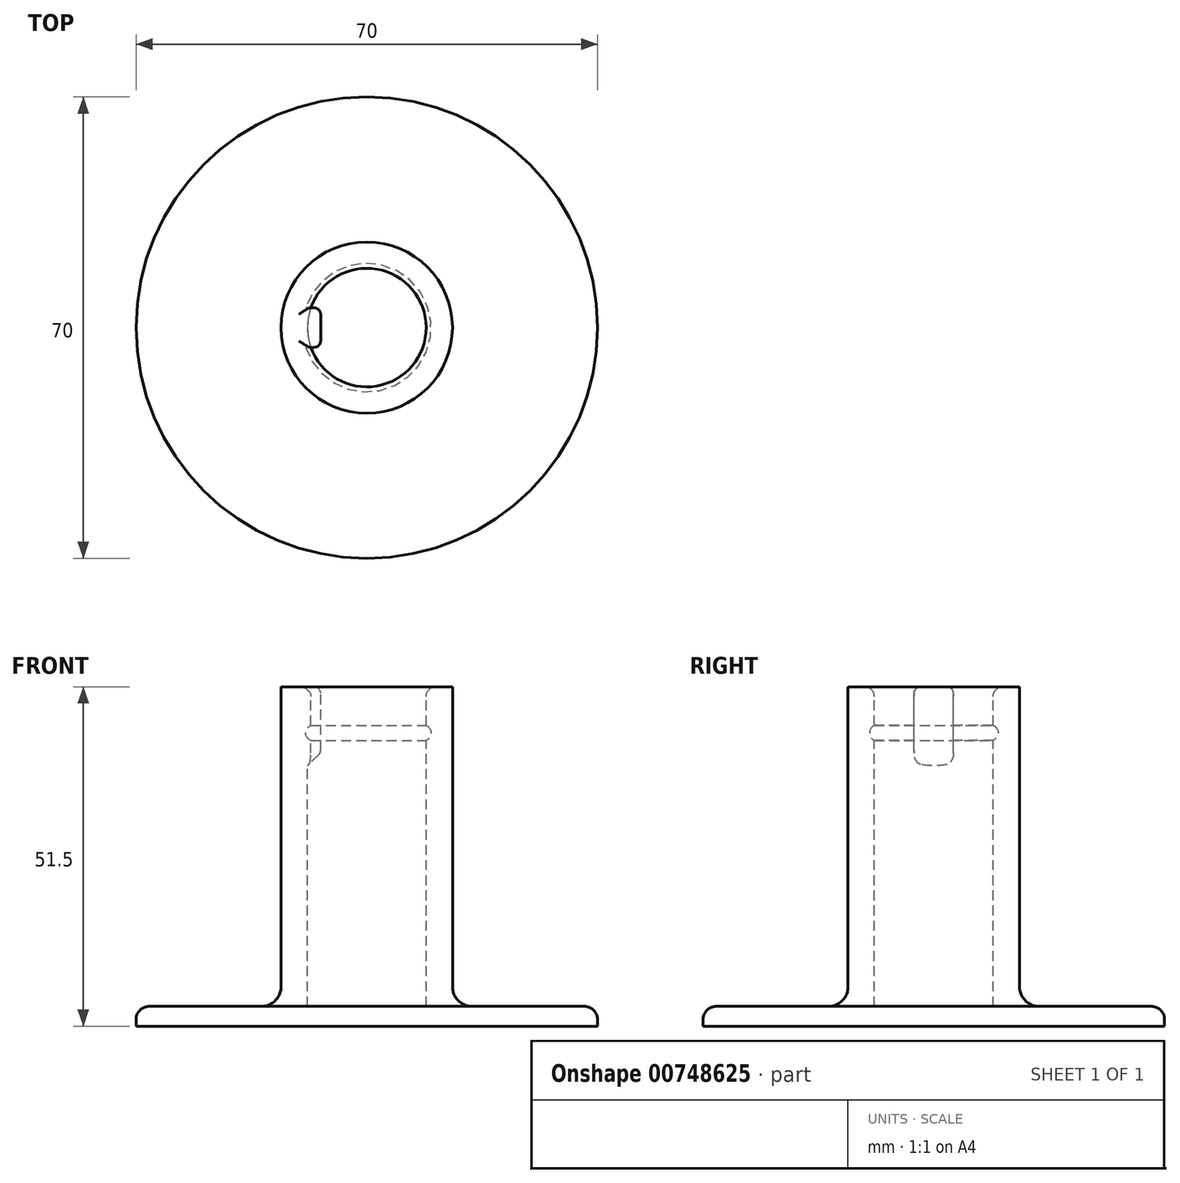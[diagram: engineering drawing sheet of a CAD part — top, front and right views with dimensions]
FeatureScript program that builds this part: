
annotation { "Feature Type Name" : "Feature", "Feature Type Description" : "" }
export const myFeature = defineFeature(function(context is Context, id is Id, definition is map)
    precondition{}
    {
        {
            var Q0;
            Q0=qCreatedBy(makeId("Front.planeOp"),FACE);
            var sketch = newSketch(context, id + "F0", { "sketchPlane" : qUnion([Q0])});
            skLineSegment(sketch, "E0.bottom", {"start": v(0, 0) * mm, "end": v(35, 0) * mm});
            skLineSegment(sketch, "E0.top", {"start": v(0, 3) * mm, "end": v(9, 3) * mm});
            skLineSegment(sketch, "E0.left", {"start": v(0, 0) * mm, "end": v(0, 3) * mm});
            skLineSegment(sketch, "E0.right", {"start": v(35, 0) * mm, "end": v(35, 1) * mm});
            skLineSegment(sketch, "E1.bottom", {"start": v(10.5, 51.5) * mm, "end": v(13, 51.5) * mm});
            skLineSegment(sketch, "E1.left", {"start": v(9, 50) * mm, "end": v(9, 45.65) * mm});
            skLineSegment(sketch, "E1.right", {"start": v(13, 51.5) * mm, "end": v(13, 6) * mm});
            skLineSegment(sketch, "E2.trimOffspring", {"start": v(16, 3) * mm, "end": v(33, 3) * mm});
            skPoint(sketch, "E3.visualSharp", {"position": v(13, 3) * mm});
            skArc(sketch, "E3.filletArc", {"start": v(13, 6) * mm, "mid": v(13.88, 3.88) * mm, "end": v(16, 3) * mm});
            skPoint(sketch, "E4.visualSharp", {"position": v(35, 3) * mm});
            skArc(sketch, "E4.filletArc", {"start": v(35, 1) * mm, "mid": v(34.41, 2.41) * mm, "end": v(33, 3) * mm});
            skArc(sketch, "E5", {"start": v(9, 43.35) * mm, "mid": v(9.75, 44.5) * mm, "end": v(9, 45.65) * mm});
            skLineSegment(sketch, "E6.trimOffspring", {"start": v(9, 43.35) * mm, "end": v(9, 3) * mm});
            skPoint(sketch, "E7.visualSharp", {"position": v(9, 51.5) * mm});
            skArc(sketch, "E7.filletArc", {"start": v(10.5, 51.5) * mm, "mid": v(9.44, 51.06) * mm, "end": v(9, 50) * mm});
            skLineSegment(sketch, "E8", {"start": v(0, 69.3) * mm, "end": v(0, -20.63) * mm, "construction": true});
            skSolve(sketch);
        }
        {
            var Q0;
            Q0 = qSketchRegion(id + "F0", true);
            var Q1;
            Q1=sQuery(id+"F0.wireOp",EDGE,"E8");
            revolve(context, id + "F1", {"surfaceOperationType" : NewSurfaceOperationType.NEW, "entities" : qUnion([Q0]), "axis" : qUnion([Q1]), "revolveType" : RevolveType.FULL});
        }
        {
            var Q0;
            Q0=makeQuery(id+"F1.opRevolve","SWEPT_FACE",FACE,{"disambiguationData":[OSD([sQuery(id+"F0.wireOp",EDGE,"E1.bottom")])]});
            var sketch = newSketch(context, id + "F2", { "sketchPlane" : qUnion([Q0])});
            skLineSegment(sketch, "E9.bottom", {"start": v(-7, 3) * mm, "end": v(-11.02, 3) * mm});
            skLineSegment(sketch, "E9.top", {"start": v(-7, -3) * mm, "end": v(-11.02, -3) * mm});
            skLineSegment(sketch, "E9.left", {"start": v(-7, 3) * mm, "end": v(-7, -3) * mm});
            skLineSegment(sketch, "E9.right", {"start": v(-11.02, 3) * mm, "end": v(-11.02, -3) * mm});
            skPoint(sketch, "E9.middle", {"position": v(-9.01, 0) * mm});
            skSolve(sketch);
        }
        {
            var Q0;
            {var subQ0=sQuery(id+"F2.wireOp",EDGE,"E9.left");Q0=makeQuery(id+"F2.imprint","IMPRINT",FACE,{"disambiguationData":[TD([[makeQuery(id+"F2.imprint","IMPRINT",EDGE,{"derivedFrom":subQ0}),-1.0]])]});}
            extrude(context, id + "F3", {"entities" : qUnion([Q0]), "operationType" : NewBodyOperationType.ADD, "oppositeDirection" : true, "depth" : 15 * mm, "offsetDistance" : 25 * mm});
        }
        {
            var Q0;
            Q0=makeQuery(id+"F3.opExtrude","CAP_EDGE",EDGE,{"disambiguationData":[OSD([sQuery(id+"F2.wireOp",EDGE,"E9.left")])],"isStart":false});
            chamfer(context, id + "F4", {"entities" : qUnion([Q0]), "width" : 5 * mm, "tangentPropagation" : true});
        }
        {
            var Q0;
            Q0=makeQuery(id+"F3.opExtrude","SWEPT_EDGE",EDGE,{"disambiguationData":[OSD([sQuery(id+"F2.wireOp",EDGE,"E9.top"),sQuery(id+"F2.wireOp",EDGE,"E9.left")])]});
            var Q1;
            Q1=makeQuery(id+"F3.opExtrude","SWEPT_EDGE",EDGE,{"disambiguationData":[OSD([sQuery(id+"F2.wireOp",EDGE,"E9.bottom"),sQuery(id+"F2.wireOp",EDGE,"E9.left")])]});
            var Q2;
            {var subQ0=sQuery(id+"F2.wireOp",EDGE,"E9.left");Q2=makeQuery(id+"F4.opChamfer","BLEND_EDGE",EDGE,{"blendedFrom":[makeQuery(id+"F3.opExtrude","CAP_EDGE",EDGE,{"disambiguationData":[OSD([subQ0])],"isStart":false}),makeQuery(id+"F3.opExtrude","SWEPT_FACE",FACE,{"disambiguationData":[OSD([subQ0])]})],"blendedInto":[makeQuery(id+"F3.opExtrude","SWEPT_FACE",FACE,{"disambiguationData":[OSD([subQ0])]})]});}
            var Q3;
            Q3=makeQuery(id+"F4.opChamfer","BLEND_EDGE",EDGE,{"blendedFrom":[makeQuery(id+"F3.opExtrude","CAP_EDGE",EDGE,{"disambiguationData":[OSD([sQuery(id+"F2.wireOp",EDGE,"E9.left")])],"isStart":false}),makeQuery(id+"F3.opExtrude","SWEPT_FACE",FACE,{"disambiguationData":[OSD([sQuery(id+"F2.wireOp",EDGE,"E9.top")])]})],"blendedInto":[makeQuery(id+"F3.opExtrude","SWEPT_FACE",FACE,{"disambiguationData":[OSD([sQuery(id+"F2.wireOp",EDGE,"E9.top")])]})]});
            var Q4;
            Q4=makeQuery(id+"F4.opChamfer","BLEND_EDGE",EDGE,{"blendedFrom":[makeQuery(id+"F3.opExtrude","CAP_EDGE",EDGE,{"disambiguationData":[OSD([sQuery(id+"F2.wireOp",EDGE,"E9.left")])],"isStart":false}),makeQuery(id+"F3.opExtrude","SWEPT_FACE",FACE,{"disambiguationData":[OSD([sQuery(id+"F2.wireOp",EDGE,"E9.bottom")])]})],"blendedInto":[makeQuery(id+"F3.opExtrude","SWEPT_FACE",FACE,{"disambiguationData":[OSD([sQuery(id+"F2.wireOp",EDGE,"E9.bottom")])]})]});
            var Q5;
            Q5=makeQuery(id+"F3.opExtrude","CAP_EDGE",EDGE,{"disambiguationData":[OSD([sQuery(id+"F2.wireOp",EDGE,"E9.left")])],"isStart":true});
            var Q6;
            Q6=makeQuery(id+"F3.opExtrude","CAP_EDGE",EDGE,{"disambiguationData":[OSD([sQuery(id+"F2.wireOp",EDGE,"E9.top")])],"isStart":true});
            var Q7;
            Q7=makeQuery(id+"F3.opExtrude","CAP_EDGE",EDGE,{"disambiguationData":[OSD([sQuery(id+"F2.wireOp",EDGE,"E9.bottom")])],"isStart":true});
            fillet(context, id + "F5", {"entities" : qUnion([Q0, Q1, Q2, Q3, Q4, Q5, Q6, Q7]), "radius" : 1 * mm, "tangentPropagation" : true, "allowEdgeOverflow" : false});
        }
    });
